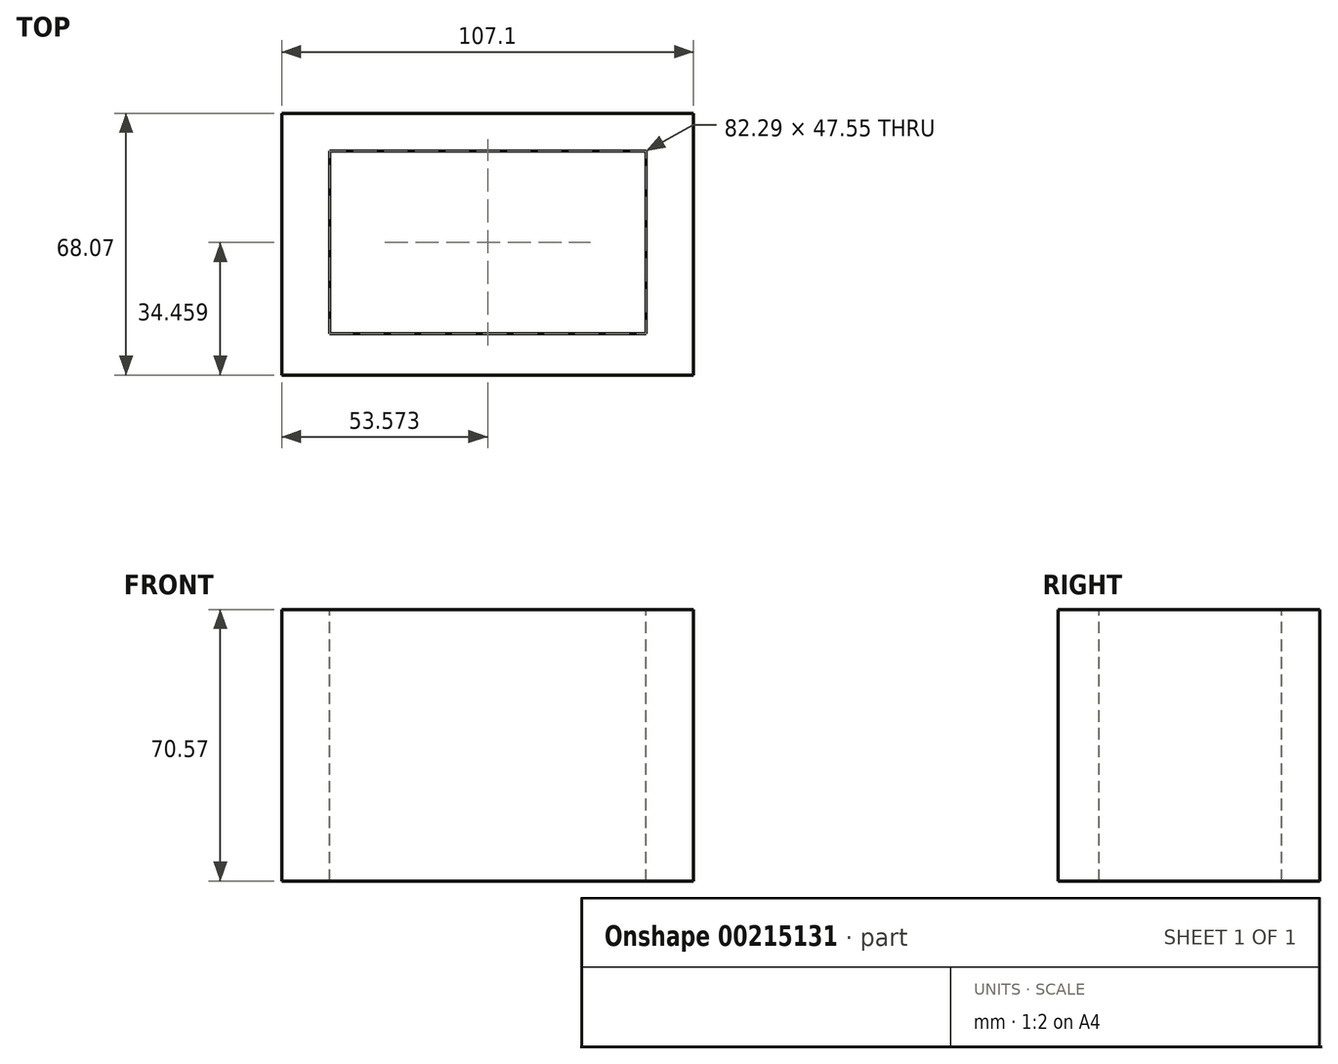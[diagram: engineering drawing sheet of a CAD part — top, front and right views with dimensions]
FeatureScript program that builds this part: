
annotation { "Feature Type Name" : "Feature", "Feature Type Description" : "" }
export const myFeature = defineFeature(function(context is Context, id is Id, definition is map)
    precondition{}
    {
        {
            var Q0;
            Q0=qCreatedBy(makeId("Front.planeOp"),FACE);
            var sketch = newSketch(context, id + "F0", { "sketchPlane" : qUnion([Q0])});
            skLineSegment(sketch, "E0.bottom", {"start": v(-53.86, 34.82) * mm, "end": v(53.24, 34.82) * mm});
            skLineSegment(sketch, "E0.top", {"start": v(-53.86, -35.75) * mm, "end": v(53.24, -35.75) * mm});
            skLineSegment(sketch, "E0.left", {"start": v(-53.86, 34.82) * mm, "end": v(-53.86, -35.75) * mm});
            skLineSegment(sketch, "E0.right", {"start": v(53.24, 34.82) * mm, "end": v(53.24, -35.75) * mm});
            skSolve(sketch);
        }
        {
            var Q0;
            Q0=makeQuery(id+"F0.imprint","IMPRINT",FACE,{"disambiguationData":[TD([[makeQuery(id+"F0.imprint","IMPRINT",EDGE,{"derivedFrom":sQuery(id+"F0.wireOp",EDGE,"E0.bottom")}),-1.0]])]});
            extrude(context, id + "F1", {"entities" : qUnion([Q0]), "oppositeDirection" : true, "depth" : 68.07 * mm});
        }
        {
            var Q0;
            Q0=makeQuery(id+"F1.opExtrude","SWEPT_FACE",FACE,{"disambiguationData":[OSD([sQuery(id+"F0.wireOp",EDGE,"E0.bottom")])]});
            var sketch = newSketch(context, id + "F2", { "sketchPlane" : qUnion([Q0])});
            skLineSegment(sketch, "E1.bottom", {"start": v(-41.43, 58.23) * mm, "end": v(40.86, 58.23) * mm});
            skLineSegment(sketch, "E1.top", {"start": v(-41.43, 10.69) * mm, "end": v(40.86, 10.69) * mm});
            skLineSegment(sketch, "E1.left", {"start": v(-41.43, 58.23) * mm, "end": v(-41.43, 10.69) * mm});
            skLineSegment(sketch, "E1.right", {"start": v(40.86, 58.23) * mm, "end": v(40.86, 10.69) * mm});
            skSolve(sketch);
        }
        {
            var Q0;
            Q0=makeQuery(id+"F2.imprint","IMPRINT",FACE,{"disambiguationData":[TD([[makeQuery(id+"F2.imprint","IMPRINT",EDGE,{"derivedFrom":sQuery(id+"F2.wireOp",EDGE,"E1.bottom")}),-1.0]])]});
            extrude(context, id + "F3", {"entities" : qUnion([Q0]), "operationType" : NewBodyOperationType.REMOVE, "oppositeDirection" : true, "depth" : 72.14 * mm});
        }
    });
